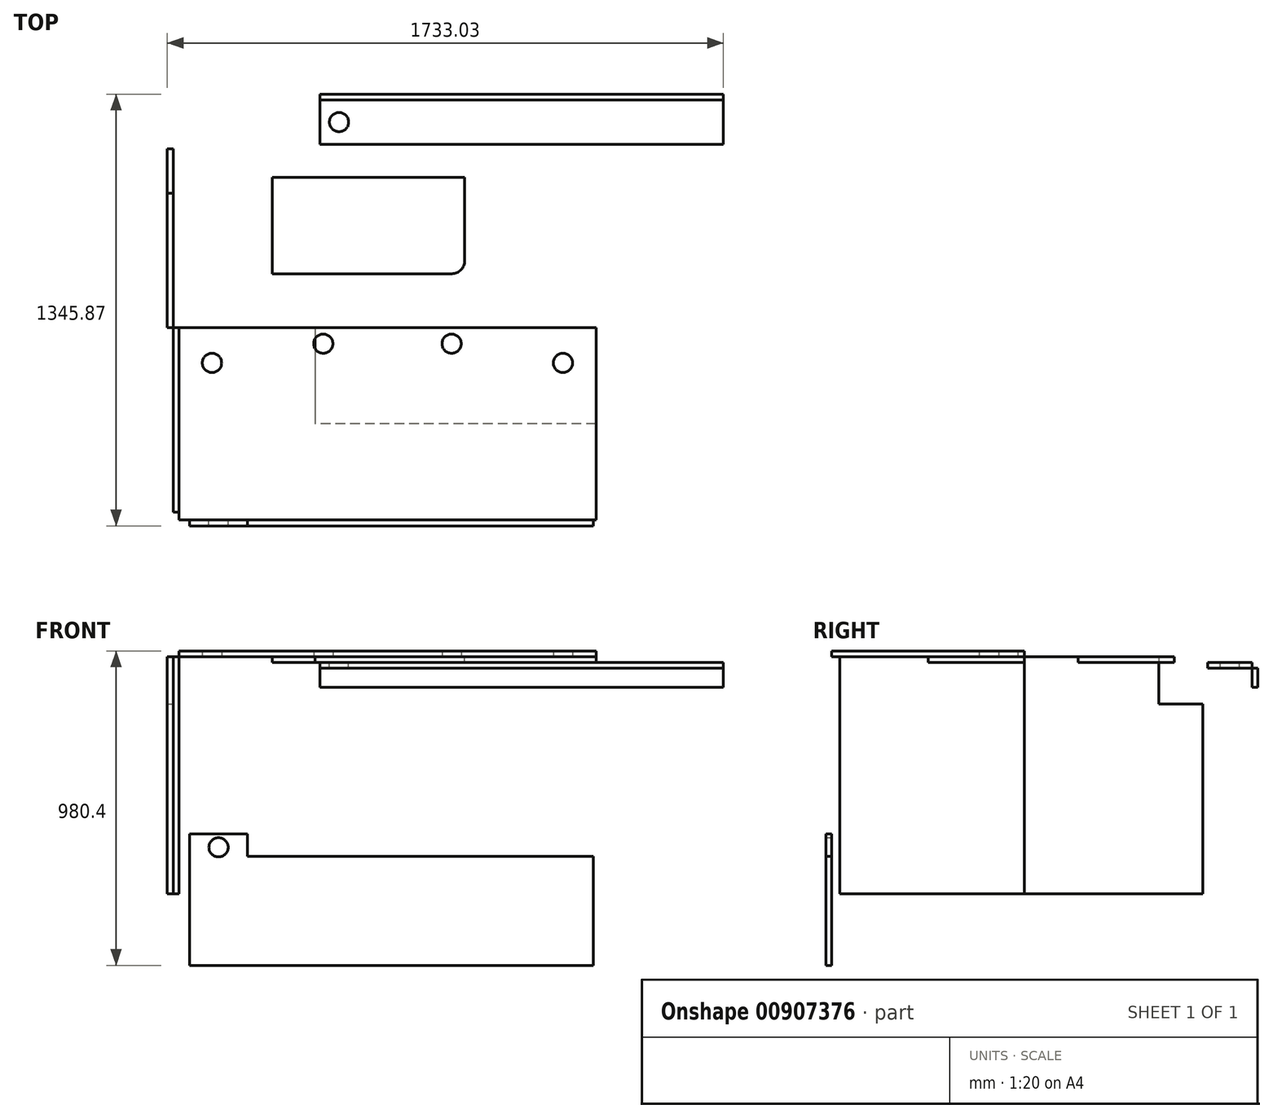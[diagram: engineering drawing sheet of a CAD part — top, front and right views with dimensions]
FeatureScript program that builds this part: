
annotation { "Feature Type Name" : "Feature", "Feature Type Description" : "" }
export const myFeature = defineFeature(function(context is Context, id is Id, definition is map)
    precondition{}
    {
        {
            var Q0;
            Q0=qCreatedBy(makeId("Top.planeOp"),FACE);
            var sketch = newSketch(context, id + "F0", { "sketchPlane" : qUnion([Q0])});
            skLineSegment(sketch, "E0.bottom", {"start": v(650, -300) * mm, "end": v(-650, -300) * mm});
            skLineSegment(sketch, "E0.top", {"start": v(650, 300) * mm, "end": v(-650, 300) * mm});
            skLineSegment(sketch, "E0.left", {"start": v(650, -300) * mm, "end": v(650, 300) * mm});
            skLineSegment(sketch, "E0.right", {"start": v(-650, -300) * mm, "end": v(-650, 300) * mm});
            skPoint(sketch, "E0.middle", {"position": v(0, 0) * mm});
            skCircle(sketch, "E1", {"center": v(-200, 250) * mm, "radius": 30 * mm});
            skCircle(sketch, "E2", {"center": v(200, 250) * mm, "radius": 30 * mm});
            skCircle(sketch, "E3", {"center": v(-547, 190) * mm, "radius": 30 * mm});
            skCircle(sketch, "E4", {"center": v(547, 190) * mm, "radius": 30 * mm});
            skSolve(sketch);
        }
        {
            var Q0;
            Q0 = qSketchRegion(id + "F0", true);
            extrude(context, id + "F1", {"entities" : qUnion([Q0]), "depth" : 18 * mm, "offsetDistance" : 25 * mm});
        }
        {
            var Q0;
            Q0=makeQuery(id+"F1.opExtrude","SWEPT_FACE",FACE,{"disambiguationData":[OSD([sQuery(id+"F0.wireOp",EDGE,"E0.right")])]});
            var sketch = newSketch(context, id + "F2", { "sketchPlane" : qUnion([Q0])});
            skLineSegment(sketch, "E5.bottom", {"start": v(-300, 0) * mm, "end": v(275, 0) * mm});
            skLineSegment(sketch, "E5.top", {"start": v(-300, -740) * mm, "end": v(275, -740) * mm});
            skLineSegment(sketch, "E5.left", {"start": v(-300, 0) * mm, "end": v(-300, -740) * mm});
            skLineSegment(sketch, "E5.right", {"start": v(275, 0) * mm, "end": v(275, -740) * mm});
            skSolve(sketch);
        }
        {
            var Q0;
            Q0 = qSketchRegion(id + "F2", true);
            extrude(context, id + "F3", {"entities" : qUnion([Q0]), "depth" : 18 * mm, "offsetDistance" : 25 * mm});
        }
        {
            var Q0;
            Q0=makeQuery(id+"F3.opExtrude","CAP_FACE",FACE,{"disambiguationData":[OSD([sQuery(id+"F2.wireOp",EDGE,"E5.bottom"),sQuery(id+"F2.wireOp",EDGE,"E5.top"),sQuery(id+"F2.wireOp",EDGE,"E5.left"),sQuery(id+"F2.wireOp",EDGE,"E5.right")])],"isStart":false});
            var sketch = newSketch(context, id + "F4", { "sketchPlane" : qUnion([Q0])});
            skLineSegment(sketch, "E6.bottom", {"start": v(-300, -740) * mm, "end": v(-857, -740) * mm});
            skLineSegment(sketch, "E6.top", {"start": v(-300, 0) * mm, "end": v(-719, 0) * mm});
            skLineSegment(sketch, "E6.left", {"start": v(-300, -740) * mm, "end": v(-300, 0) * mm});
            skLineSegment(sketch, "E6.right", {"start": v(-857, -740) * mm, "end": v(-857, -148) * mm});
            skLineSegment(sketch, "E7", {"start": v(-719, 0) * mm, "end": v(-719, -148) * mm});
            skLineSegment(sketch, "E8", {"start": v(-719, -148) * mm, "end": v(-857, -148) * mm});
            skPoint(sketch, "E9.orphan", {"position": v(-857, 0) * mm});
            skSolve(sketch);
        }
        {
            var Q0;
            Q0 = qSketchRegion(id + "F4", true);
            extrude(context, id + "F5", {"entities" : qUnion([Q0]), "depth" : 18 * mm, "offsetDistance" : 25 * mm});
        }
        {
            var Q0;
            Q0=makeQuery(id+"F1.opExtrude","CAP_FACE",FACE,{"disambiguationData":[OSD([sQuery(id+"F0.wireOp",EDGE,"E0.bottom"),sQuery(id+"F0.wireOp",EDGE,"E0.top"),sQuery(id+"F0.wireOp",EDGE,"E0.left"),sQuery(id+"F0.wireOp",EDGE,"E0.right"),sQuery(id+"F0.wireOp",EDGE,"E1"),sQuery(id+"F0.wireOp",EDGE,"E2"),sQuery(id+"F0.wireOp",EDGE,"E3"),sQuery(id+"F0.wireOp",EDGE,"E4")])],"isStart":true});
            var sketch = newSketch(context, id + "F6", { "sketchPlane" : qUnion([Q0])});
            skLineSegment(sketch, "E10.bottom", {"start": v(-359.27, -468.1) * mm, "end": v(200.73, -468.1) * mm});
            skLineSegment(sketch, "E10.top", {"start": v(-359.27, -768.1) * mm, "end": v(240.73, -768.1) * mm});
            skLineSegment(sketch, "E10.left", {"start": v(-359.27, -468.1) * mm, "end": v(-359.27, -768.1) * mm});
            skLineSegment(sketch, "E10.right", {"start": v(240.73, -508.1) * mm, "end": v(240.73, -768.1) * mm});
            skPoint(sketch, "E11.visualSharp", {"position": v(240.73, -468.1) * mm});
            skArc(sketch, "E11.filletArc", {"start": v(240.73, -508.1) * mm, "mid": v(229.02, -479.81) * mm, "end": v(200.73, -468.1) * mm});
            skSolve(sketch);
        }
        {
            var Q0;
            Q0 = qSketchRegion(id + "F6", true);
            extrude(context, id + "F7", {"entities" : qUnion([Q0]), "depth" : 18 * mm, "offsetDistance" : 25 * mm});
        }
        {
            var Q0;
            Q0=makeQuery(id+"F1.opExtrude","SWEPT_FACE",FACE,{"disambiguationData":[OSD([sQuery(id+"F0.wireOp",EDGE,"E0.bottom")])]});
            var sketch = newSketch(context, id + "F8", { "sketchPlane" : qUnion([Q0])});
            skLineSegment(sketch, "E12.bottom", {"start": v(-436.62, -622.4) * mm, "end": v(641.38, -622.4) * mm});
            skLineSegment(sketch, "E12.top", {"start": v(-616.62, -962.4) * mm, "end": v(641.38, -962.4) * mm});
            skLineSegment(sketch, "E12.right", {"start": v(641.38, -622.4) * mm, "end": v(641.38, -962.4) * mm});
            skLineSegment(sketch, "E13", {"start": v(-616.62, -552.4) * mm, "end": v(-436.62, -552.4) * mm});
            skLineSegment(sketch, "E14", {"start": v(-436.62, -552.4) * mm, "end": v(-436.62, -622.4) * mm});
            skLineSegment(sketch, "E15", {"start": v(-616.62, -552.4) * mm, "end": v(-616.62, -962.4) * mm});
            skCircle(sketch, "E16", {"center": v(-526.62, -594.4) * mm, "radius": 30 * mm});
            skSolve(sketch);
        }
        {
            var Q0;
            Q0 = qSketchRegion(id + "F8", true);
            extrude(context, id + "F9", {"entities" : qUnion([Q0]), "depth" : 18 * mm, "offsetDistance" : 25 * mm});
        }
        {
            var Q0;
            Q0=makeQuery(id+"F1.opExtrude","CAP_FACE",FACE,{"disambiguationData":[OSD([sQuery(id+"F0.wireOp",EDGE,"E0.bottom"),sQuery(id+"F0.wireOp",EDGE,"E0.top"),sQuery(id+"F0.wireOp",EDGE,"E0.left"),sQuery(id+"F0.wireOp",EDGE,"E0.right"),sQuery(id+"F0.wireOp",EDGE,"E1"),sQuery(id+"F0.wireOp",EDGE,"E2"),sQuery(id+"F0.wireOp",EDGE,"E3"),sQuery(id+"F0.wireOp",EDGE,"E4")])],"isStart":true});
            var sketch = newSketch(context, id + "F10", { "sketchPlane" : qUnion([Q0])});
            skLineSegment(sketch, "E17.bottom", {"start": v(650, -300) * mm, "end": v(-226, -300) * mm});
            skLineSegment(sketch, "E17.top", {"start": v(650, 0) * mm, "end": v(-226, 0) * mm});
            skLineSegment(sketch, "E17.left", {"start": v(650, -300) * mm, "end": v(650, 0) * mm});
            skLineSegment(sketch, "E17.right", {"start": v(-226, -300) * mm, "end": v(-226, 0) * mm});
            skSolve(sketch);
        }
        {
            var Q0;
            Q0 = qSketchRegion(id + "F10", true);
            extrude(context, id + "F11", {"entities" : qUnion([Q0]), "depth" : 18 * mm, "offsetDistance" : 25 * mm});
        }
        {
            var Q0;
            Q0=makeQuery(id+"F11.opExtrude","CAP_FACE",FACE,{"disambiguationData":[OSD([sQuery(id+"F10.wireOp",EDGE,"E17.bottom"),sQuery(id+"F10.wireOp",EDGE,"E17.top"),sQuery(id+"F10.wireOp",EDGE,"E17.left"),sQuery(id+"F10.wireOp",EDGE,"E17.right")])],"isStart":false});
            var sketch = newSketch(context, id + "F12", { "sketchPlane" : qUnion([Q0])});
            skLineSegment(sketch, "E18.bottom", {"start": v(-210.97, -871.87) * mm, "end": v(1047.03, -871.87) * mm});
            skLineSegment(sketch, "E18.top", {"start": v(-210.97, -1009.87) * mm, "end": v(1047.03, -1009.87) * mm});
            skLineSegment(sketch, "E18.left", {"start": v(-210.97, -871.87) * mm, "end": v(-210.97, -1009.87) * mm});
            skLineSegment(sketch, "E18.right", {"start": v(1047.03, -871.87) * mm, "end": v(1047.03, -1009.87) * mm});
            skCircle(sketch, "E19", {"center": v(-150.97, -940.87) * mm, "radius": 30 * mm});
            skPoint(sketch, "E19.centerSnap0", {"position": v(-210.97, -940.87) * mm});
            skSolve(sketch);
        }
        {
            var Q0;
            Q0 = qSketchRegion(id + "F12", true);
            extrude(context, id + "F13", {"entities" : qUnion([Q0]), "depth" : 18 * mm, "offsetDistance" : 25 * mm});
        }
        {
            var Q0;
            Q0=makeQuery(id+"F13.opExtrude","SWEPT_FACE",FACE,{"disambiguationData":[OSD([sQuery(id+"F12.wireOp",EDGE,"E18.top")])]});
            var sketch = newSketch(context, id + "F14", { "sketchPlane" : qUnion([Q0])});
            skLineSegment(sketch, "E20.bottom", {"start": v(-1047.03, -36) * mm, "end": v(210.97, -36) * mm});
            skLineSegment(sketch, "E20.top", {"start": v(-1047.03, -96) * mm, "end": v(210.97, -96) * mm});
            skLineSegment(sketch, "E20.left", {"start": v(-1047.03, -36) * mm, "end": v(-1047.03, -96) * mm});
            skLineSegment(sketch, "E20.right", {"start": v(210.97, -36) * mm, "end": v(210.97, -96) * mm});
            skSolve(sketch);
        }
        {
            var Q0;
            Q0 = qSketchRegion(id + "F14", true);
            extrude(context, id + "F15", {"entities" : qUnion([Q0]), "depth" : 18 * mm, "offsetDistance" : 25 * mm});
        }
    });
